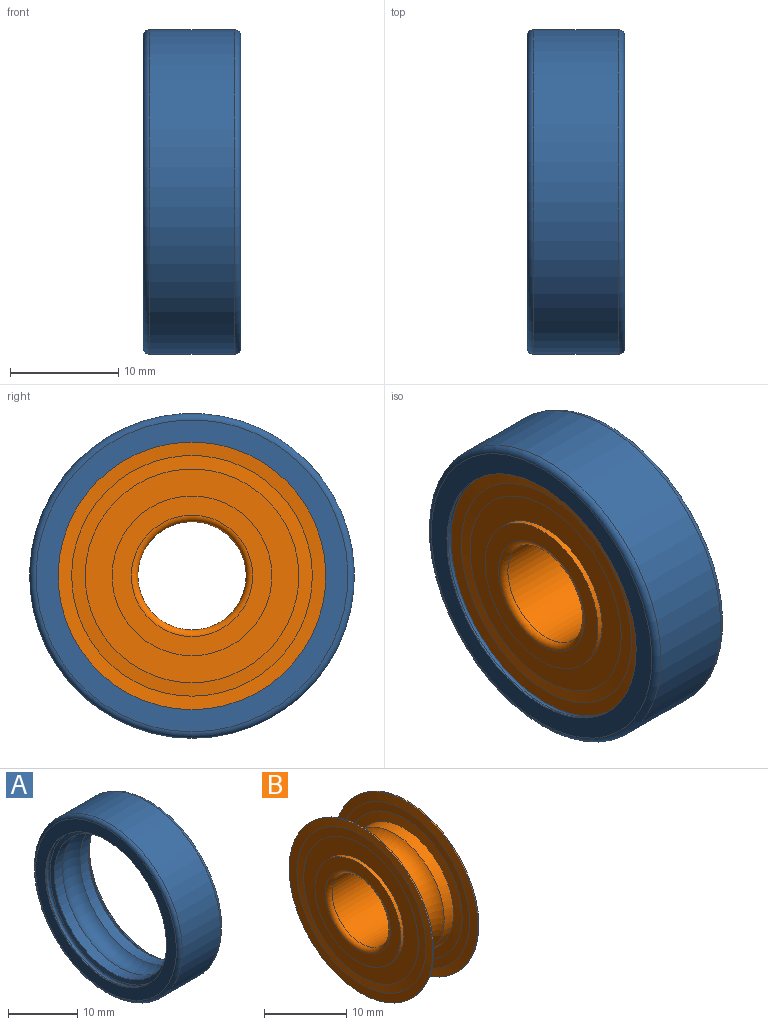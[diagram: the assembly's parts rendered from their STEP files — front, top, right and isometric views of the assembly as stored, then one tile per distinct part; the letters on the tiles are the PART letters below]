
ASSEMBLY  parts=2 mates=1
PART A: 14 faces, bbox 9x32.5x32.5 mm
  f0: plane 28.8x28.8mm, normal (-1,0,0), area 171.5mm2, adj f1,f13
  f1: cylinder r=12.36mm len=24.72mm, axis (-1,0,0), area 14mm2, adj f0,f2
  f2: torus R=12.36mm, axis (1,0,0), area 89.5mm2, adj f1,f3
  f3: cone r=12.36mm half-angle=80deg, axis (-1,0,0), area 58.1mm2, adj f2,f4
  f4: cylinder r=11.6mm len=23.2mm, axis (-1,0,0), area 124.1mm2, adj f3,f5
  f5: torus R=10mm, axis (1,0,0), area 302.3mm2, adj f4,f6
  f6: cylinder r=11.6mm len=23.2mm, axis (-1,0,0), area 124.1mm2, adj f5,f7
  f7: cone r=11.6mm half-angle=80deg, axis (1,0,0), area 58.1mm2, adj f6,f8
  f8: torus R=12.36mm, axis (1,0,0), area 89.5mm2, adj f7,f9
  f9: cylinder r=12.36mm len=24.72mm, axis (-1,0,0), area 14mm2, adj f8,f10
  f10: plane 28.8x28.8mm, normal (1,0,0), area 171.5mm2, adj f9,f11
  f11: torus R=14.4mm, axis (1,0,0), area 87.5mm2, adj f10,f12
  f12: cylinder r=15mm len=30mm, axis (-1,0,0), area 735.1mm2, adj f11,f13
  f13: torus R=14.4mm, axis (1,0,0), area 87.5mm2, adj f0,f12
PART B: 28 faces, bbox 9x24.7x24.7 mm
  f0: cone r=12.36mm half-angle=81.8deg, axis (1,0,0), area 92.9mm2, adj f1,f27
  f1: plane 22.23x22.23mm, normal (-1,0,0), area 82.1mm2, adj f0,f2
  f2: cone r=9.87mm half-angle=85.9deg, axis (-1,0,0), area 134.1mm2, adj f1,f15
  f3: plane 14.75x14.75mm, normal (-1,0,0), area 72.4mm2, adj f5,f12
  f4: plane 14.75x14.75mm, normal (1,0,0), area 72.4mm2, adj f7,f13
  f5: cylinder r=7.38mm len=14.75mm, axis (-1,0,0), area 25mm2, adj f3,f20
  f6: torus R=7.83mm, axis (1,0,0), area 26.3mm2, adj f16,f21
  f7: torus R=5.6mm, axis (1,0,0), area 30.9mm2, adj f4,f11
  f8: cylinder r=8.5mm len=17mm, axis (-1,0,0), area 87.1mm2, adj f9,f16
  f9: torus R=10mm, axis (1,0,0), area 210.7mm2, adj f8,f10
  f10: cylinder r=8.5mm len=17mm, axis (-1,0,0), area 87.1mm2, adj f9,f14
  f11: cylinder r=5mm len=10mm, axis (-1,0,0), area 245mm2, adj f7,f12
  f12: torus R=5.6mm, axis (1,0,0), area 30.9mm2, adj f3,f11
  f13: cylinder r=7.38mm len=14.75mm, axis (-1,0,0), area 25mm2, adj f4,f24
  f14: plane 17x17mm, normal (1,0,0), area 34.6mm2, adj f10,f15
  f15: torus R=7.83mm, axis (1,0,0), area 26.3mm2, adj f2,f14
  f16: plane 17x17mm, normal (-1,0,0), area 34.6mm2, adj f6,f8
  f17: cylinder r=12.36mm len=24.72mm, axis (-1,0,0), area 14mm2, adj f18,f23
  f18: cone r=12.36mm half-angle=85.9deg, axis (-1,0,0), area 92.1mm2, adj f17,f19
  f19: cone r=11.11mm half-angle=85.9deg, axis (1,0,0), area 82.4mm2, adj f18,f20
  f20: plane 19.74x19.74mm, normal (-1,0,0), area 135mm2, adj f5,f19
  f21: cone r=7.38mm half-angle=85.9deg, axis (1,0,0), area 134.1mm2, adj f6,f22
  f22: plane 22.23x22.23mm, normal (1,0,0), area 82.1mm2, adj f21,f23
  f23: cone r=11.11mm half-angle=81.8deg, axis (-1,0,0), area 92.9mm2, adj f17,f22
  f24: plane 19.74x19.74mm, normal (1,0,0), area 135mm2, adj f13,f25
  f25: cone r=9.87mm half-angle=85.9deg, axis (-1,0,0), area 82.4mm2, adj f24,f26
  f26: cone r=11.11mm half-angle=85.9deg, axis (1,0,0), area 92.1mm2, adj f25,f27
  f27: cylinder r=12.36mm len=24.72mm, axis (-1,0,0), area 14mm2, adj f0,f26
PLACE A at identity
PLACE B at identity
MATE fastened A.f1 <-> B.f0  axis (1,0,0) through (4.5,0,0)mm
